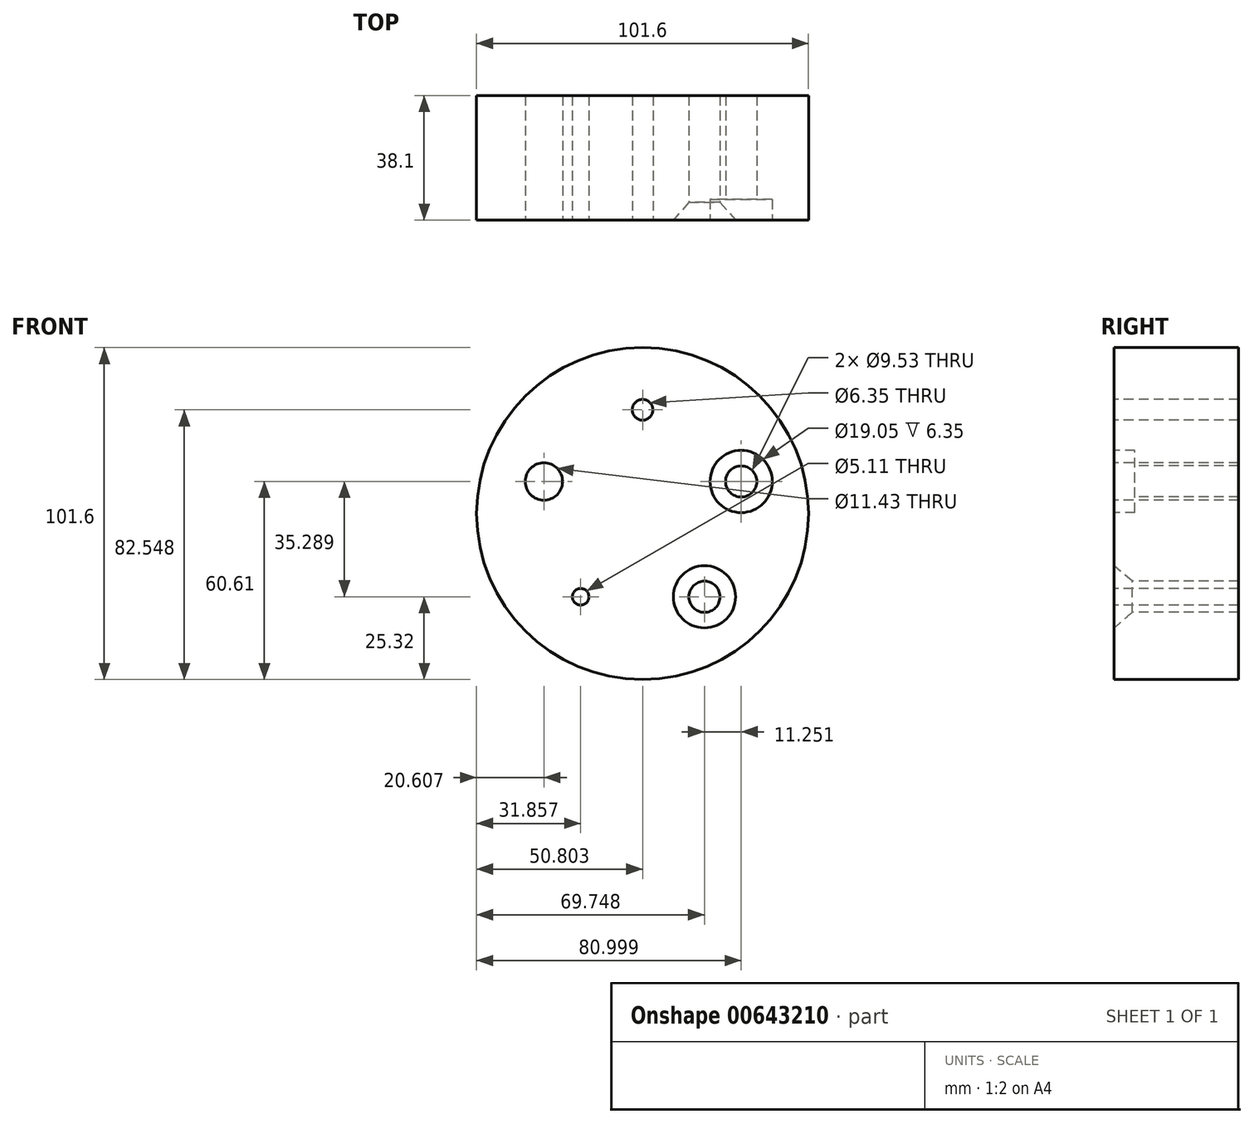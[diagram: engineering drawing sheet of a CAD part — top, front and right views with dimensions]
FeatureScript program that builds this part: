
annotation { "Feature Type Name" : "Feature", "Feature Type Description" : "" }
export const myFeature = defineFeature(function(context is Context, id is Id, definition is map)
    precondition{}
    {
        {
            var Q0;
            Q0=qCreatedBy(makeId("Front.planeOp"),FACE);
            var sketch = newSketch(context, id + "F0", { "sketchPlane" : qUnion([Q0])});
            skCircle(sketch, "E0", {"center": v(-1.06, 7.13) * mm, "radius": 50.8 * mm});
            skCircle(sketch, "E1", {"center": v(-1.06, 7.13) * mm, "radius": 31.75 * mm, "construction": true});
            skLineSegment(sketch, "E2", {"start": v(-1.06, 7.13) * mm, "end": v(-1.06, 75.54) * mm, "construction": true});
            skLineSegment(sketch, "E3", {"start": v(-1.06, 7.13) * mm, "end": v(-66.12, 28.27) * mm, "construction": true});
            skLineSegment(sketch, "E4", {"start": v(8.55, 7.13) * mm, "end": v(-10.54, 7.13) * mm, "construction": true});
            skCircle(sketch, "E5", {"center": v(-1.06, 38.88) * mm, "radius": 3.18 * mm});
            skPoint(sketch, "E5.centerSnap0", {"position": v(-1.06, 41.33) * mm});
            skCircle(sketch, "E6", {"center": v(-31.25, 16.94) * mm, "radius": 5.72 * mm});
            skCircle(sketch, "E7", {"center": v(29.14, 16.94) * mm, "radius": 9.53 * mm});
            skCircle(sketch, "E8", {"center": v(29.14, 16.94) * mm, "radius": 4.76 * mm});
            skCircle(sketch, "E9", {"center": v(17.89, -18.35) * mm, "radius": 9.53 * mm});
            skCircle(sketch, "E10", {"center": v(17.89, -18.35) * mm, "radius": 4.76 * mm});
            skCircle(sketch, "E11", {"center": v(-20, -18.35) * mm, "radius": 1.59 * mm});
            skSolve(sketch);
        }
        {
            var Q0;
            Q0=makeQuery(id+"F0.imprint","IMPRINT",FACE,{"disambiguationData":[TD([[makeQuery(id+"F0.imprint","IMPRINT",EDGE,{"derivedFrom":sQuery(id+"F0.wireOp",EDGE,"E5")}),1.0]])]});
            var Q1;
            Q1=makeQuery(id+"F0.imprint","IMPRINT",FACE,{"disambiguationData":[TD([[makeQuery(id+"F0.imprint","IMPRINT",EDGE,{"derivedFrom":sQuery(id+"F0.wireOp",EDGE,"E6")}),1.0]])]});
            var Q2;
            Q2=makeQuery(id+"F0.imprint","IMPRINT",FACE,{"disambiguationData":[TD([[makeQuery(id+"F0.imprint","IMPRINT",EDGE,{"derivedFrom":sQuery(id+"F0.wireOp",EDGE,"E8")}),1.0]])]});
            var Q3;
            Q3=makeQuery(id+"F0.imprint","IMPRINT",FACE,{"disambiguationData":[TD([[makeQuery(id+"F0.imprint","IMPRINT",EDGE,{"derivedFrom":sQuery(id+"F0.wireOp",EDGE,"E10")}),1.0]])]});
            var Q4;
            Q4=makeQuery(id+"F0.imprint","IMPRINT",FACE,{"disambiguationData":[TD([[makeQuery(id+"F0.imprint","IMPRINT",EDGE,{"derivedFrom":sQuery(id+"F0.wireOp",EDGE,"E11")}),1.0]])]});
            var Q5;
            Q5=makeQuery(id+"F0.imprint","IMPRINT",FACE,{"disambiguationData":[TD([[makeQuery(id+"F0.imprint","IMPRINT",EDGE,{"derivedFrom":sQuery(id+"F0.wireOp",EDGE,"E7")}),1.0]])]});
            var Q6;
            Q6=makeQuery(id+"F0.imprint","IMPRINT",FACE,{"disambiguationData":[TD([[makeQuery(id+"F0.imprint","IMPRINT",EDGE,{"derivedFrom":sQuery(id+"F0.wireOp",EDGE,"E9")}),1.0]])]});
            var Q7;
            Q7=makeQuery(id+"F0.imprint","IMPRINT",FACE,{"disambiguationData":[TD([[makeQuery(id+"F0.imprint","IMPRINT",EDGE,{"derivedFrom":sQuery(id+"F0.wireOp",EDGE,"E0")}),1.0]])]});
            extrude(context, id + "F1", {"entities" : qUnion([Q0, Q1, Q2, Q3, Q4, Q5, Q6, Q7]), "oppositeDirection" : true, "depth" : 38.1 * mm, "offsetDistance" : 25.4 * mm});
        }
        {
            var Q0;
            Q0=sQuery(id+"F0.wireOp",VERTEX,"E5.center");
            var Q1;
            Q1=makeQuery(id+"F1.opExtrude","SWEPT_BODY",BODY,{"disambiguationData":[OSD([sQuery(id+"F0.wireOp",EDGE,"E0")])]});
            hole(context, id + "F2", {"style" : HoleStyle.SIMPLE, "endStyle" : HoleEndStyle.THROUGH, "holeDiameter" : 6.35 * mm, "majorDiameter" : 6.35 * mm, "isTappedThrough" : true, "tappedDepth" : 12.7 * mm, "tapClearance" : 3, "locations" : qUnion([Q0]), "scope" : qUnion([Q1])});
        }
        {
            var Q0;
            Q0=sQuery(id+"F0.wireOp",VERTEX,"E8.center");
            var Q1;
            Q1=makeQuery(id+"F1.opExtrude","SWEPT_BODY",BODY,{"disambiguationData":[OSD([sQuery(id+"F0.wireOp",EDGE,"E0")])]});
            hole(context, id + "F3", {"style" : HoleStyle.C_BORE, "endStyle" : HoleEndStyle.THROUGH, "holeDiameter" : 9.52 * mm, "cBoreDiameter" : 19.05 * mm, "cBoreDepth" : 6.35 * mm, "majorDiameter" : 6.35 * mm, "isTappedThrough" : true, "tappedDepth" : 12.7 * mm, "tapClearance" : 3, "locations" : qUnion([Q0]), "scope" : qUnion([Q1])});
        }
        {
            var Q0;
            Q0=sQuery(id+"F0.wireOp",VERTEX,"E10.center");
            var Q1;
            Q1=makeQuery(id+"F1.opExtrude","SWEPT_BODY",BODY,{"disambiguationData":[OSD([sQuery(id+"F0.wireOp",EDGE,"E0")])]});
            hole(context, id + "F4", {"style" : HoleStyle.C_SINK, "endStyle" : HoleEndStyle.THROUGH, "holeDiameter" : 9.52 * mm, "cSinkDiameter" : 19.05 * mm, "cSinkAngle" : 82 * degree, "majorDiameter" : 6.35 * mm, "isTappedThrough" : true, "tappedDepth" : 12.7 * mm, "tapClearance" : 3, "locations" : qUnion([Q0]), "scope" : qUnion([Q1])});
        }
        {
            var Q0;
            Q0=sQuery(id+"F0.wireOp",VERTEX,"E11.center");
            var Q1;
            Q1=makeQuery(id+"F1.opExtrude","SWEPT_BODY",BODY,{"disambiguationData":[OSD([sQuery(id+"F0.wireOp",EDGE,"E0")])]});
            hole(context, id + "F5", {"style" : HoleStyle.SIMPLE, "endStyle" : HoleEndStyle.BLIND, "standardTappedOrClearance" : lookupTablePath({ "standard" : "ANSI", "engagement" : "75%", "pitch" : "20 tpi", "size" : "1/4", "type" : "Tapped" }), "standardBlindInLast" : lookupTablePath({ "standard" : "ANSI", "engagement" : "75%", "pitch" : "20 tpi", "size" : "1/4", "type" : "Tapped" }), "holeDiameter" : 5.1 * mm, "majorDiameter" : 6.35 * mm, "showTappedDepth" : true, "holeDepth" : 38.1 * mm, "isTappedThrough" : true, "tappedDepth" : 34.3 * mm, "tapClearance" : 3, "locations" : qUnion([Q0]), "scope" : qUnion([Q1])});
        }
        {
            var Q0;
            Q0=sQuery(id+"F0.wireOp",VERTEX,"E6.center");
            var Q1;
            Q1=makeQuery(id+"F1.opExtrude","SWEPT_BODY",BODY,{"disambiguationData":[OSD([sQuery(id+"F0.wireOp",EDGE,"E0")])]});
            hole(context, id + "F6", {"style" : HoleStyle.SIMPLE, "endStyle" : HoleEndStyle.THROUGH, "holeDiameter" : 11.43 * mm, "majorDiameter" : 6.35 * mm, "isTappedThrough" : true, "tappedDepth" : 34.3 * mm, "tapClearance" : 3, "locations" : qUnion([Q0]), "scope" : qUnion([Q1])});
        }
    });
